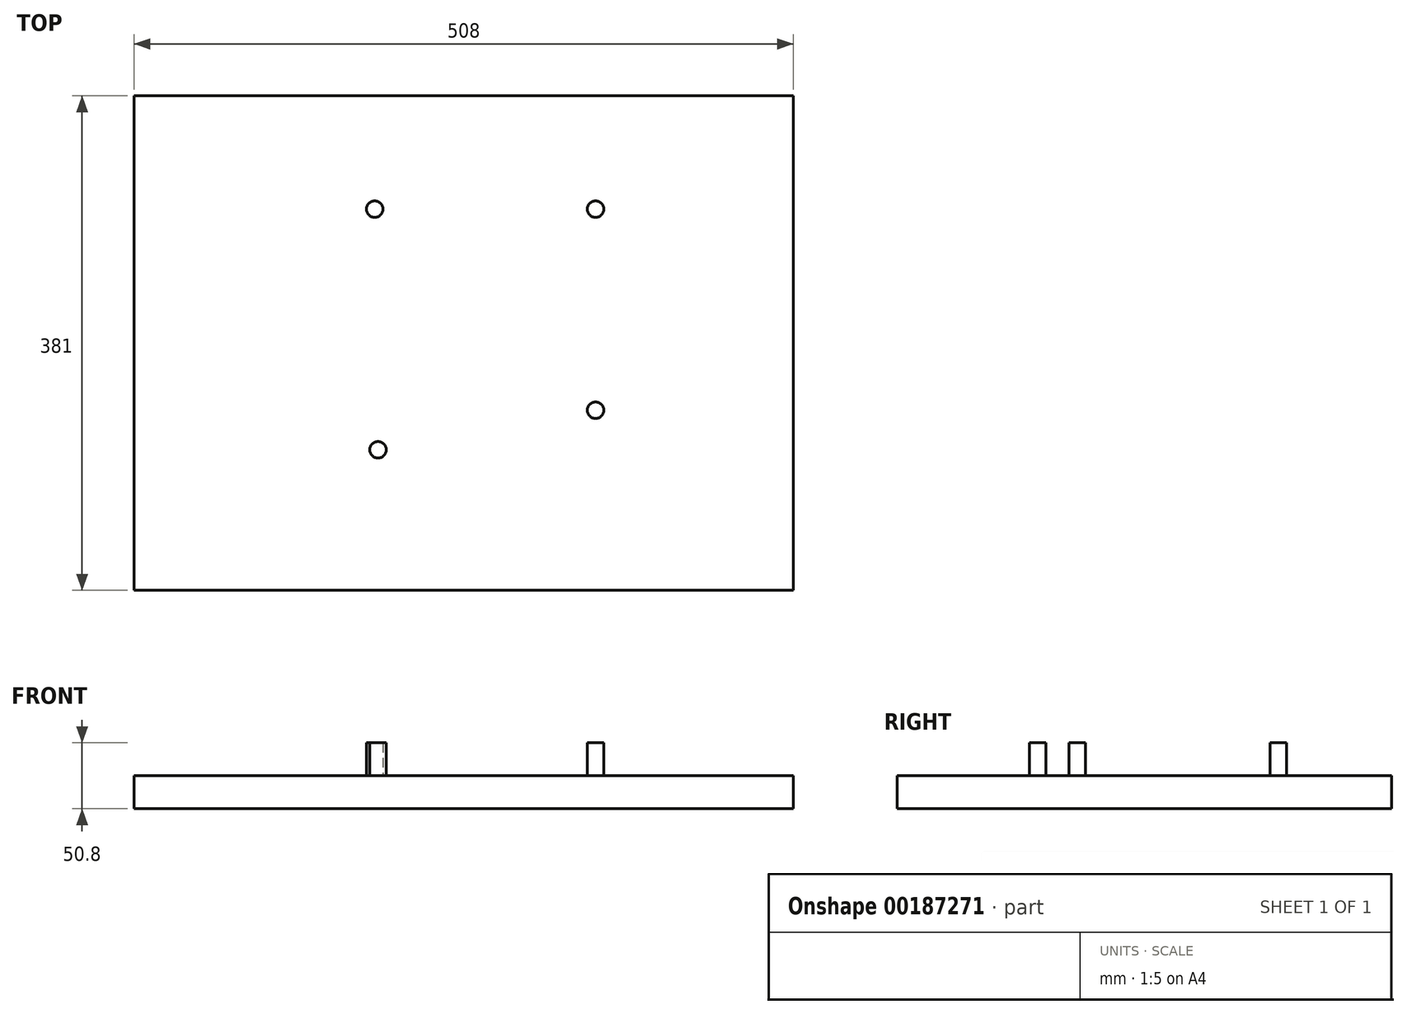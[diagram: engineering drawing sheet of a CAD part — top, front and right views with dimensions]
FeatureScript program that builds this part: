
annotation { "Feature Type Name" : "Feature", "Feature Type Description" : "" }
export const myFeature = defineFeature(function(context is Context, id is Id, definition is map)
    precondition{}
    {
        {
            var Q0;
            Q0=qCreatedBy(makeId("Top.planeOp"),FACE);
            var sketch = newSketch(context, id + "F0", { "sketchPlane" : qUnion([Q0])});
            skLineSegment(sketch, "E0.bottom", {"start": v(-238.06, 242.2) * mm, "end": v(269.94, 242.2) * mm});
            skLineSegment(sketch, "E0.top", {"start": v(-238.06, -138.8) * mm, "end": v(269.94, -138.8) * mm});
            skLineSegment(sketch, "E0.left", {"start": v(-238.06, 242.2) * mm, "end": v(-238.06, -138.8) * mm});
            skLineSegment(sketch, "E0.right", {"start": v(269.94, 242.2) * mm, "end": v(269.94, -138.8) * mm});
            skSolve(sketch);
        }
        {
            var Q0;
            Q0=makeQuery(id+"F0.imprint","IMPRINT",FACE,{"disambiguationData":[TD([[makeQuery(id+"F0.imprint","IMPRINT",EDGE,{"derivedFrom":sQuery(id+"F0.wireOp",EDGE,"E0.bottom")}),-1.0]])]});
            extrude(context, id + "F1", {"entities" : qUnion([Q0]), "depth" : 25.4 * mm});
        }
        {
            var Q0;
            Q0=makeQuery(id+"F1.opExtrude","CAP_FACE",FACE,{"disambiguationData":[OSD([sQuery(id+"F0.wireOp",EDGE,"E0.bottom"),sQuery(id+"F0.wireOp",EDGE,"E0.top"),sQuery(id+"F0.wireOp",EDGE,"E0.left"),sQuery(id+"F0.wireOp",EDGE,"E0.right")])],"isStart":false});
            var sketch = newSketch(context, id + "F2", { "sketchPlane" : qUnion([Q0])});
            skCircle(sketch, "E1", {"center": v(-52.64, 154.94) * mm, "radius": 6.35 * mm});
            skCircle(sketch, "E2", {"center": v(117.54, 154.94) * mm, "radius": 6.35 * mm});
            skCircle(sketch, "E3", {"center": v(117.54, 0) * mm, "radius": 6.35 * mm});
            skCircle(sketch, "E4", {"center": v(-50.1, -30.48) * mm, "radius": 6.35 * mm});
            skSolve(sketch);
        }
        {
            var Q0;
            Q0=makeQuery(id+"F2.imprint","IMPRINT",FACE,{"disambiguationData":[TD([[makeQuery(id+"F2.imprint","IMPRINT",EDGE,{"derivedFrom":sQuery(id+"F2.wireOp",EDGE,"E1")}),1.0]])]});
            var Q1;
            Q1=makeQuery(id+"F2.imprint","IMPRINT",FACE,{"disambiguationData":[TD([[makeQuery(id+"F2.imprint","IMPRINT",EDGE,{"derivedFrom":sQuery(id+"F2.wireOp",EDGE,"yGOtU5F1-CgMw-EoCN-OVoP-L3xPvfaENLJE")}),1.0]])]});
            var Q2;
            Q2=makeQuery(id+"F2.imprint","IMPRINT",FACE,{"disambiguationData":[TD([[makeQuery(id+"F2.imprint","IMPRINT",EDGE,{"derivedFrom":sQuery(id+"F2.wireOp",EDGE,"E2")}),1.0]])]});
            var Q3;
            Q3=makeQuery(id+"F2.imprint","IMPRINT",FACE,{"disambiguationData":[TD([[makeQuery(id+"F2.imprint","IMPRINT",EDGE,{"derivedFrom":sQuery(id+"F2.wireOp",EDGE,"E3")}),1.0]])]});
            extrude(context, id + "F3", {"entities" : qUnion([Q0, Q1, Q2, Q3]), "operationType" : NewBodyOperationType.ADD, "depth" : 25.4 * mm});
        }
        {
            var Q0;
            Q0 = qSketchRegion(id + "F2", true);
            var Q1;
            Q1=makeQuery(id+"F1.opExtrude","CAP_FACE",FACE,{"disambiguationData":[OSD([sQuery(id+"F0.wireOp",EDGE,"E0.bottom"),sQuery(id+"F0.wireOp",EDGE,"E0.top"),sQuery(id+"F0.wireOp",EDGE,"E0.left"),sQuery(id+"F0.wireOp",EDGE,"E0.right")])],"isStart":true});
            extrude(context, id + "F4", {"entities" : qUnion([Q0, Q1]), "operationType" : NewBodyOperationType.ADD, "depth" : 25.4 * mm});
        }
        {
            var Q0;
            Q0 = qSketchRegion(id + "F2", true);
            var Q1;
            Q1=makeQuery(id+"F1.opExtrude","CAP_FACE",FACE,{"disambiguationData":[OSD([sQuery(id+"F0.wireOp",EDGE,"E0.bottom"),sQuery(id+"F0.wireOp",EDGE,"E0.top"),sQuery(id+"F0.wireOp",EDGE,"E0.left"),sQuery(id+"F0.wireOp",EDGE,"E0.right")])],"isStart":true});
            extrude(context, id + "F5", {"entities" : qUnion([Q0, Q1]), "operationType" : NewBodyOperationType.ADD, "depth" : 25.4 * mm});
        }
    });
